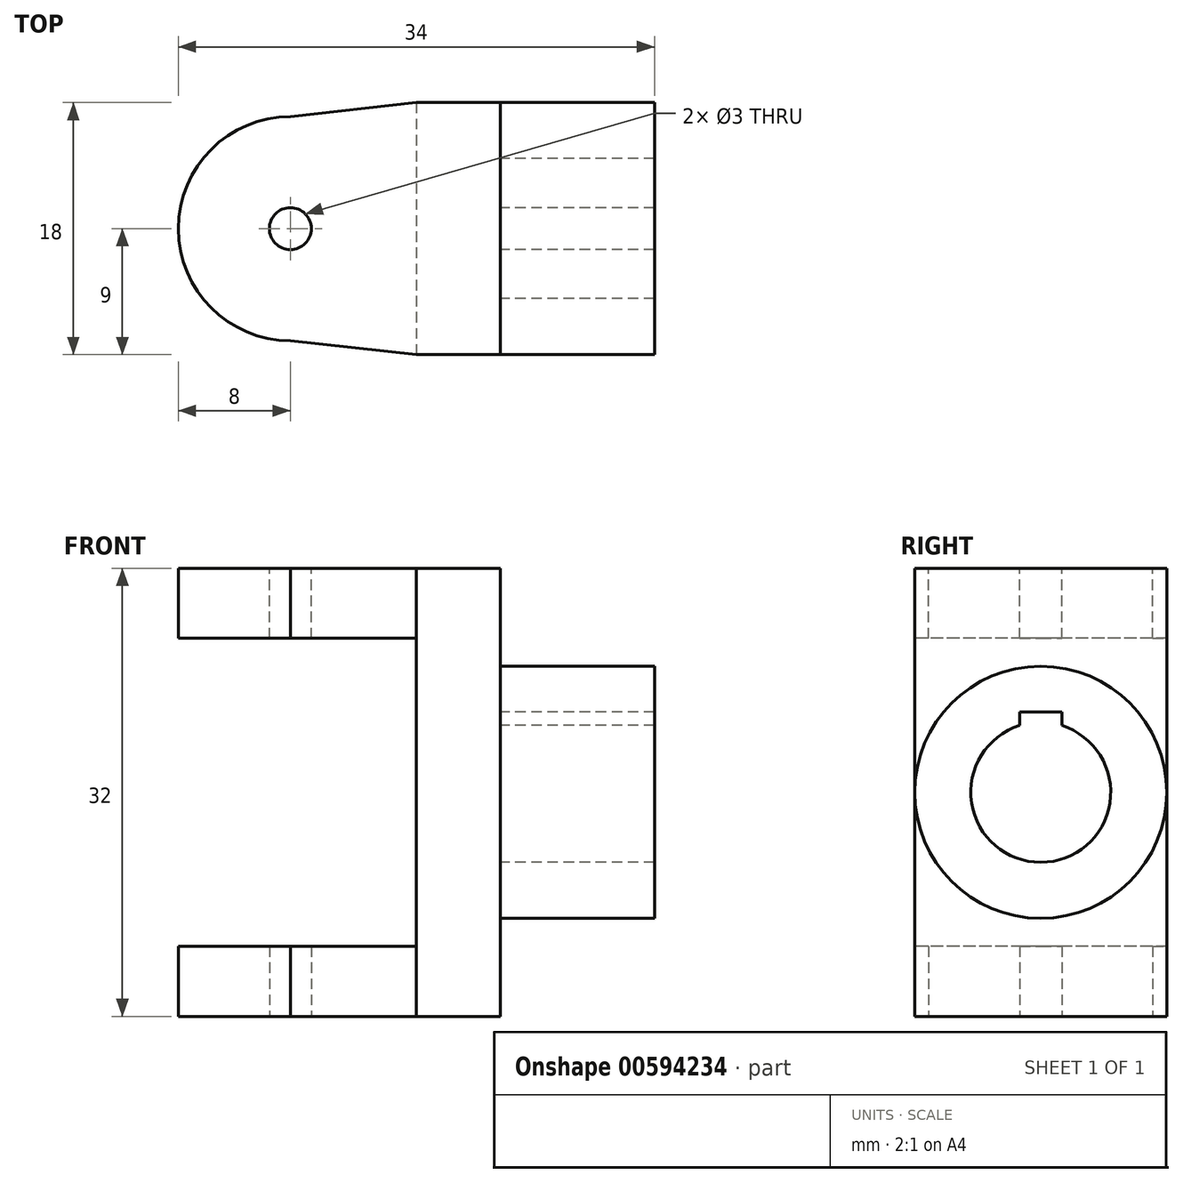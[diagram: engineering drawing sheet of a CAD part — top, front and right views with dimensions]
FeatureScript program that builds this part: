
annotation { "Feature Type Name" : "Feature", "Feature Type Description" : "" }
export const myFeature = defineFeature(function(context is Context, id is Id, definition is map)
    precondition{}
    {
        {
            var Q0;
            Q0=qCreatedBy(makeId("Right.planeOp"),FACE);
            var sketch = newSketch(context, id + "F0", { "sketchPlane" : qUnion([Q0])});
            skLineSegment(sketch, "E0.bottom", {"start": v(9, -16) * mm, "end": v(-9, -16) * mm});
            skLineSegment(sketch, "E0.top", {"start": v(9, 16) * mm, "end": v(-9, 16) * mm});
            skLineSegment(sketch, "E0.left", {"start": v(9, -16) * mm, "end": v(9, 16) * mm});
            skLineSegment(sketch, "E0.right", {"start": v(-9, -16) * mm, "end": v(-9, 16) * mm});
            skPoint(sketch, "E0.middle", {"position": v(0, 0) * mm});
            skSolve(sketch);
        }
        {
            var Q0;
            Q0=makeQuery(id+"F0.imprint","IMPRINT",FACE,{"disambiguationData":[TD([[makeQuery(id+"F0.imprint","IMPRINT",EDGE,{"derivedFrom":sQuery(id+"F0.wireOp",EDGE,"E0.bottom")}),-1.0]])]});
            extrude(context, id + "F1", {"entities" : qUnion([Q0]), "oppositeDirection" : true, "depth" : 6 * mm, "offsetDistance" : 25.4 * mm});
        }
        {
            var Q0;
            Q0=makeQuery(id+"F1.opExtrude","SWEPT_FACE",FACE,{"disambiguationData":[OSD([sQuery(id+"F0.wireOp",EDGE,"E0.top")])]});
            var sketch = newSketch(context, id + "F2", { "sketchPlane" : qUnion([Q0])});
            skArc(sketch, "E1", {"start": v(-15, 8) * mm, "mid": v(-23, 0) * mm, "end": v(-15, -8) * mm});
            skLineSegment(sketch, "E2", {"start": v(-15, -8) * mm, "end": v(-6, -9) * mm});
            skLineSegment(sketch, "E3", {"start": v(-15, 8) * mm, "end": v(-6, 9) * mm});
            skCircle(sketch, "E4", {"center": v(-15, 0) * mm, "radius": 1.5 * mm});
            skSolve(sketch);
        }
        {
            var Q0;
            Q0=makeQuery(id+"F2.imprint","IMPRINT",FACE,{"disambiguationData":[TD([[makeQuery(id+"F2.imprint","IMPRINT",EDGE,{"derivedFrom":sQuery(id+"F2.wireOp",EDGE,"E1")}),1.0]])]});
            extrude(context, id + "F3", {"entities" : qUnion([Q0]), "operationType" : NewBodyOperationType.ADD, "oppositeDirection" : true, "depth" : 5 * mm, "offsetDistance" : 25.4 * mm});
        }
        {
            var Q0;
            Q0=makeQuery(id+"F1.opExtrude","SWEPT_BODY",BODY,{"disambiguationData":[OSD([sQuery(id+"F0.wireOp",EDGE,"E0.bottom"),sQuery(id+"F0.wireOp",EDGE,"E0.top"),sQuery(id+"F0.wireOp",EDGE,"E0.left"),sQuery(id+"F0.wireOp",EDGE,"E0.right")])]});
            var Q1;
            Q1=qCreatedBy(makeId("Top.planeOp"),FACE);
            mirror(context, id + "F4", {"operationType" : NewBodyOperationType.ADD, "entities" : qUnion([Q0]), "mirrorPlane" : qUnion([Q1])});
        }
        {
            var Q0;
            Q0=makeQuery(id+"F1.opExtrude","CAP_FACE",FACE,{"disambiguationData":[OSD([sQuery(id+"F0.wireOp",EDGE,"E0.bottom"),sQuery(id+"F0.wireOp",EDGE,"E0.top"),sQuery(id+"F0.wireOp",EDGE,"E0.left"),sQuery(id+"F0.wireOp",EDGE,"E0.right")])],"isStart":true});
            var sketch = newSketch(context, id + "F5", { "sketchPlane" : qUnion([Q0])});
            skCircle(sketch, "E5", {"center": v(0, 0) * mm, "radius": 9 * mm});
            skArc(sketch, "E6", {"start": v(-1.5, 4.77) * mm, "mid": v(0, -5) * mm, "end": v(1.5, 4.77) * mm});
            skLineSegment(sketch, "E7.top", {"start": v(1.5, 5.75) * mm, "end": v(-1.5, 5.75) * mm});
            skLineSegment(sketch, "E7.left", {"start": v(1.5, 4.77) * mm, "end": v(1.5, 5.75) * mm});
            skLineSegment(sketch, "E7.right", {"start": v(-1.5, 4.77) * mm, "end": v(-1.5, 5.75) * mm});
            skPoint(sketch, "E8.start.orphan", {"position": v(0, 7.28) * mm});
            skSolve(sketch);
        }
        {
            var Q0;
            Q0 = qSketchRegion(id + "F5", true);
            extrude(context, id + "F6", {"entities" : qUnion([Q0]), "operationType" : NewBodyOperationType.ADD, "depth" : 11 * mm, "offsetDistance" : 25.4 * mm});
        }
    });
